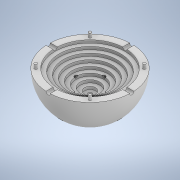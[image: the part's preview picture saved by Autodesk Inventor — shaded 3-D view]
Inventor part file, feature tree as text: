
AUTODESK INVENTOR PART (.ipt)
format: ipt  version: 2022 (Build 260153000, 153)  size: 350,208 bytes
history: native  units: mm
features: extrude x16, sketch x16, fillet x4, other x1
ambient origin geometry x8: Origin, YZ Plane, XZ Plane, XY Plane, X Axis, Y Axis, Z Axis, Center Point
bodies: Body1 (feature_tree)
feature tree (37):
  other  "實體1"
  extrude  "擠出1"  Depth=60.0mm
  fillet  "圓角1"  Radius=30.0mm
  extrude  "擠出2"  Depth=30.0mm
  extrude  "擠出3"  Depth=50.0mm
  extrude  "擠出4"  Depth=2.0mm TaperAngle=0.0deg
  extrude  "擠出5"  Depth=44.0mm
  extrude  "擠出6"  Depth=2.0mm TaperAngle=0.0deg
  extrude  "擠出7"  Depth=38.0mm
  extrude  "擠出8"  Depth=2.0mm TaperAngle=0.0deg
  extrude  "擠出9"  Depth=32.0mm
  extrude  "擠出11"  Depth=2.0mm TaperAngle=0.0deg
  extrude  "擠出12"  Depth=26.0mm
  extrude  "擠出13"  Depth=2.0mm TaperAngle=0.0deg
  extrude  "擠出16"  Depth=20.0mm
  fillet  "圓角2"  Radius=2.0mm
  extrude  "擠出17"  Depth=14.0mm
  fillet  "圓角3"  Radius=2.0mm
  extrude  "擠出18"  Depth=8.0mm
  fillet  "圓角4"  Radius=2.0mm
  extrude  "擠出19"  Depth=3.0mm
  sketch  "草圖3"
  sketch  "草圖4"
  sketch  "草圖5"
  sketch  "草圖6"
  sketch  "草圖7"
  sketch  "草圖8"
  sketch  "草圖9"
  sketch  "草圖10"
  sketch  "草圖11"
  sketch  "草圖14"
  sketch  "草圖15"
  sketch  "草圖16"
  sketch  "草圖25"
  sketch  "草圖26"
  sketch  "草圖27"
  sketch  "草圖29"
